# Revit family: APL Residential Thermal Heart Sliding Door SF with Overlight
name_source: partatom
category: Doors
revit_build: Autodesk Revit LT 2017 (Build: 20160225_1515(x64)
units: mm (PartAtom-declared; Revit-internal decimal feet)

## family parameters
Always vertical = Yes
Cut with Voids When Loaded = No
Host = Wall
OmniClass Number = 23.30.10.00
OmniClass Title = Doors
Room Calculation Point = No
Shared = No

## types (2) — shared parameters
Analytic Construction = <None>
Architrave = Yes
Arrow Opening = Yes
Awning = 400 mm  [stored 1.31234 ft]
Frame Projection Ext. = 13 mm
Frame Projection Int. = 20 mm  [stored 0.0656168 ft]
Frame Width = 17 mm
Frame Width Sill = 15 mm  [stored 0.0492126 ft]
Function = Interior
Height = 2601 mm
Jamb Liner 1 = Yes
Jamb Liner 2 = Yes
Liner Head = Yes
Reveal Liner = No
Rough Height = 2613 mm  [stored 8.57283 ft]
Rough Width = 2415 mm  [stored 7.92323 ft]
Wall Closure = By host
Width = 2400 mm  [stored 7.87402 ft]

## per-type parameters (varying)
| type | Liner Sill |
| Liner | Yes |
| Architrave | No |

note: [stored X ft] marks values corroborated as IEEE doubles in the binary element streams (Revit-internal decimal feet)

## geometry (parser evidence)
native form markers: Sweep x47
no freeform markers — native parametric forms only
